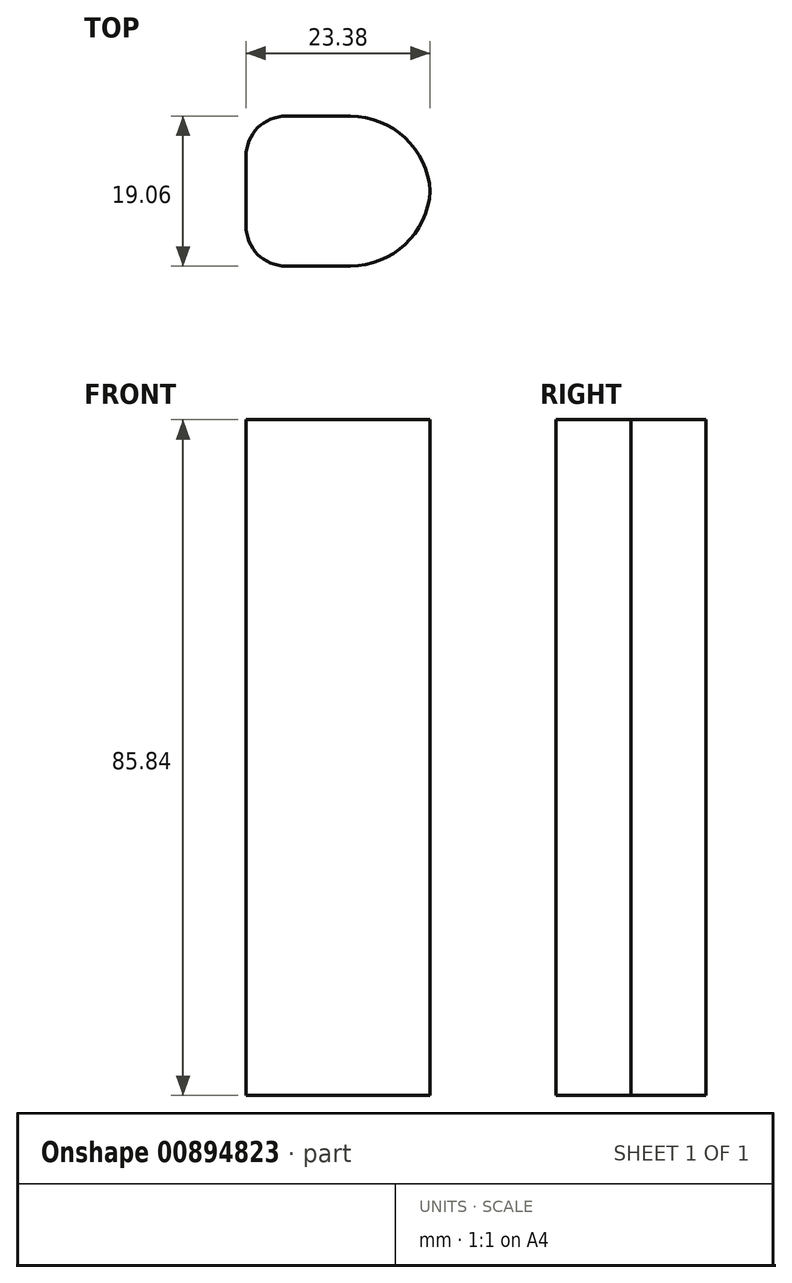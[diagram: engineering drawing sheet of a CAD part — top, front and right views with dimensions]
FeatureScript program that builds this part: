
annotation { "Feature Type Name" : "Feature", "Feature Type Description" : "" }
export const myFeature = defineFeature(function(context is Context, id is Id, definition is map)
    precondition{}
    {
        {
            var Q0;
            Q0=qCreatedBy(makeId("Front.planeOp"),FACE);
            var sketch = newSketch(context, id + "F0", { "sketchPlane" : qUnion([Q0])});
            skLineSegment(sketch, "E0", {"start": v(-12.93, 10.97) * mm, "end": v(10.47, 10.97) * mm});
            skLineSegment(sketch, "E1", {"start": v(10.47, 10.97) * mm, "end": v(71.69, 10.97) * mm});
            skFitSpline(sketch, "E2", {"points": [v(71.69, 10.97) * mm, v(75.78, 13.93) * mm, v(81.93, 17.32) * mm], "startDerivative": vector(8.34, 6.51) * mm, "endDerivative": vector(12.04, 6.2) * mm});
            skFitSpline(sketch, "E3", {"points": [v(81.93, 17.32) * mm, v(75.65, 5.53) * mm, v(68.2, -9.39) * mm, v(62.77, -26) * mm, v(59.88, -40.59) * mm, v(58.7, -55.68) * mm, v(60.1, -75.05) * mm, v(64.21, -91.12) * mm, v(70.6, -107.34) * mm, v(78.37, -121.96) * mm], "startDerivative": vector(-60.52, -114.31) * mm, "endDerivative": vector(72.3, -127.63) * mm});
            skFitSpline(sketch, "E4", {"points": [v(78.37, -121.96) * mm, v(71.69, -118.58) * mm, v(66.35, -113.98) * mm], "startDerivative": vector(-13.76, 5.98) * mm, "endDerivative": vector(-10.28, 9.98) * mm});
            skLineSegment(sketch, "E5", {"start": v(66.35, -113.98) * mm, "end": v(-2.33, -113.98) * mm});
            skLineSegment(sketch, "E6", {"start": v(-12.93, 10.97) * mm, "end": v(-12.93, -113.98) * mm});
            skLineSegment(sketch, "E7", {"start": v(-12.93, -113.98) * mm, "end": v(-2.33, -113.98) * mm});
            skFitSpline(sketch, "E8", {"points": [v(52.5, -9.73) * mm, v(44.42, -26.85) * mm, v(39.6, -44.93) * mm, v(39.24, -58.43) * mm, v(41.21, -73.26) * mm, v(44.64, -84.35) * mm, v(50.72, -95.57) * mm], "startDerivative": vector(-46.13, -88.67) * mm, "endDerivative": vector(43.2, -73.22) * mm});
            skLineSegment(sketch, "E9", {"start": v(52.5, -9.73) * mm, "end": v(10.47, -9.73) * mm});
            skLineSegment(sketch, "E10", {"start": v(50.72, -95.57) * mm, "end": v(10.47, -95.57) * mm});
            skLineSegment(sketch, "E11", {"start": v(10.47, -95.57) * mm, "end": v(10.47, -9.73) * mm});
            skLineSegment(sketch, "E12", {"start": v(-12.93, -113.98) * mm, "end": v(-12.93, -186.32) * mm});
            skLineSegment(sketch, "E13", {"start": v(-12.93, -186.32) * mm, "end": v(-1.82, -199.95) * mm});
            skLineSegment(sketch, "E14", {"start": v(-2.33, -113.98) * mm, "end": v(-2.33, -106.8) * mm});
            skLineSegment(sketch, "E15.MirrorCS", {"start": v(8.28, -113.98) * mm, "end": v(8.28, -186.32) * mm});
            skLineSegment(sketch, "E16.MirrorCS", {"start": v(8.28, -186.32) * mm, "end": v(-2.84, -199.95) * mm});
            skLineSegment(sketch, "E17", {"start": v(10.47, -9.73) * mm, "end": v(-12.93, -9.73) * mm});
            skLineSegment(sketch, "E18", {"start": v(10.47, -95.57) * mm, "end": v(-12.93, -95.57) * mm});
            skSolve(sketch);
        }
        {
            var Q0;
            {var subQ4=sQuery(id+"F0.wireOp",EDGE,"E7");Q0=makeQuery(id+"F0.imprint","IMPRINT",FACE,{"disambiguationData":[TD([[makeQuery(id+"F0.imprint","IMPRINT",EDGE,{"derivedFrom":subQ4}),-1.0]])]});}
            var Q1;
            Q1=makeQuery(id+"F0.imprint","IMPRINT",FACE,{"disambiguationData":[TD([[makeQuery(id+"F0.imprint","IMPRINT",EDGE,{"derivedFrom":sQuery(id+"F0.wireOp",EDGE,"E11")}),1.0]])]});
            extrude(context, id + "F1", {"entities" : qUnion([Q0, Q1]), "endBound" : BoundingType.SYMMETRIC, "depth" : 19.05 * mm, "offsetDistance" : 25.4 * mm});
        }
        {
            var Q0;
            Q0=makeQuery(id+"F1.opExtrude","SWEPT_BODY",BODY,{"disambiguationData":[OSD([sQuery(id+"F0.wireOp",EDGE,"E5"),sQuery(id+"F0.wireOp",EDGE,"E7"),sQuery(id+"F0.wireOp",EDGE,"E12"),sQuery(id+"F0.wireOp",EDGE,"E13"),sQuery(id+"F0.wireOp",EDGE,"E15.MirrorCS"),sQuery(id+"F0.wireOp",EDGE,"E16.MirrorCS")])]});
            deleteBodies(context, id + "F2", {"entities" : qUnion([Q0])});
        }
        {
            var Q0;
            Q0=makeQuery(id+"F1.opExtrude","CAP_EDGE",EDGE,{"disambiguationData":[OSD([sQuery(id+"F0.wireOp",EDGE,"E11")])],"isStart":false});
            var Q1;
            Q1=makeQuery(id+"F1.opExtrude","CAP_EDGE",EDGE,{"disambiguationData":[OSD([sQuery(id+"F0.wireOp",EDGE,"E11")])],"isStart":true});
            fillet(context, id + "F3", {"entities" : qUnion([Q0, Q1]), "radius" : 10.16 * mm, "tangentPropagation" : true, "allowEdgeOverflow" : false});
        }
        {
            var Q0;
            Q0=makeQuery(id+"F1.opExtrude","CAP_EDGE",EDGE,{"disambiguationData":[OSD([sQuery(id+"F0.wireOp",EDGE,"E6")])],"isStart":true});
            var Q1;
            Q1=makeQuery(id+"F1.opExtrude","CAP_EDGE",EDGE,{"disambiguationData":[OSD([sQuery(id+"F0.wireOp",EDGE,"E6")])],"isStart":false});
            fillet(context, id + "F4", {"entities" : qUnion([Q0, Q1]), "radius" : 5.08 * mm, "tangentPropagation" : true, "allowEdgeOverflow" : false});
        }
    });
